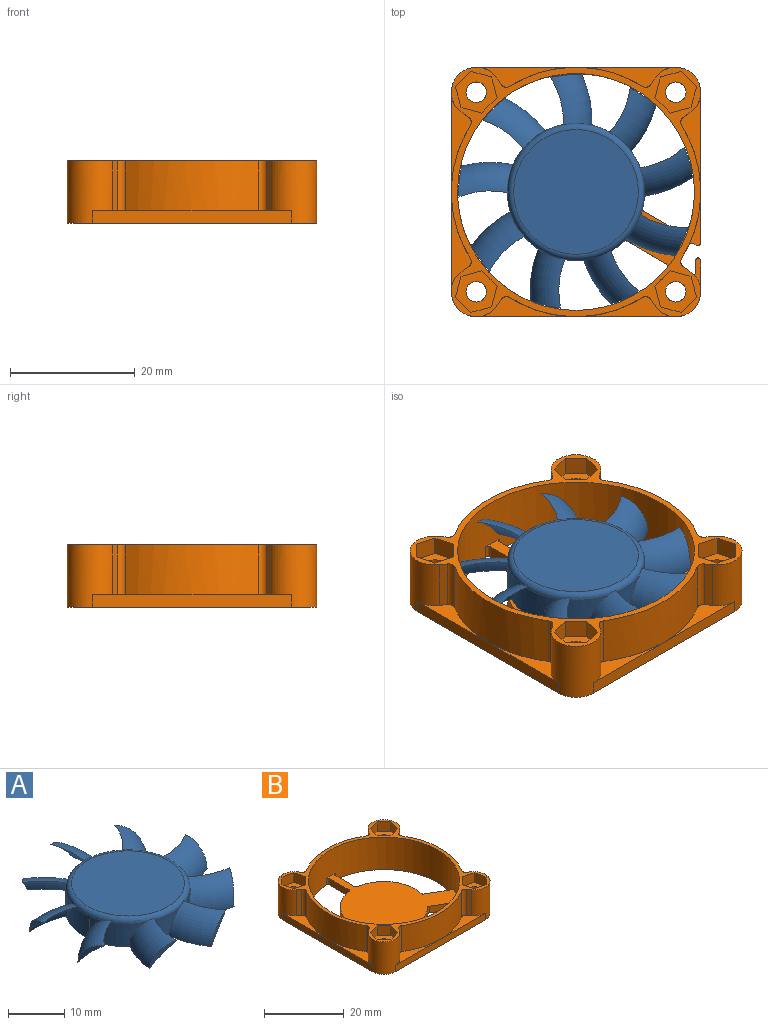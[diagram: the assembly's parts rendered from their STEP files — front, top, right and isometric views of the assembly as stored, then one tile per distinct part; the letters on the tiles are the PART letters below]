
ASSEMBLY  parts=2 mates=1
PART A: 32 faces, bbox 42.3x42.5x6 mm
  f0: cylinder r=11mm len=22mm, axis (0,0,-1), area 307.6mm2, adj f1,f3,f4,f5,f6,f8,f9,f11
  f1: cylinder r=11mm len=4.52mm, axis (0,0,-1), area 3.9mm2, adj f0,f4,f11
  f2: plane 20x20mm, normal (0,0,1), area 314.2mm2, adj f4
  f3: plane 22x22mm, normal (0,0,-1), area 380.1mm2, adj f0
  f4: torus R=10mm, axis (0,0,1), area 102.2mm2, adj f0,f1,f2,f5,f6,f8,f9,f11
  f5: torus R=12.73mm, axis (0,0,-1), area 60.3mm2, adj f0,f4,f6,f7
  f6: torus R=5.4mm, axis (0,0,-1), area 55.4mm2, adj f0,f4,f5,f7
  f7: cylinder r=18.8mm len=4.97mm, axis (0,0,1), area 4.5mm2, adj f5,f6
  f8: torus R=12.73mm, axis (0,0,-1), area 60.3mm2, adj f0,f4,f9,f10
  f9: torus R=5.4mm, axis (0,0,-1), area 55.4mm2, adj f0,f4,f8,f10
  f10: cylinder r=18.8mm len=4.97mm, axis (0,0,1), area 4.5mm2, adj f8,f9
  f11: torus R=12.73mm, axis (0,0,-1), area 60.3mm2, adj f0,f1,f4,f12,f13
  f12: torus R=5.4mm, axis (0,0,-1), area 55.4mm2, adj f0,f4,f11,f13
  f13: cylinder r=18.8mm len=4.97mm, axis (0,0,1), area 4.5mm2, adj f11,f12
  f14: torus R=12.73mm, axis (0,0,-1), area 60.3mm2, adj f0,f4,f15,f16
  f15: torus R=5.4mm, axis (0,0,-1), area 55.4mm2, adj f0,f4,f14,f16
  f16: cylinder r=18.8mm len=4.97mm, axis (0,0,1), area 4.5mm2, adj f14,f15
  f17: torus R=12.73mm, axis (0,0,-1), area 60.3mm2, adj f0,f4,f18,f19
  f18: torus R=5.4mm, axis (0,0,-1), area 55.4mm2, adj f0,f4,f17,f19
  f19: cylinder r=18.8mm len=4.97mm, axis (0,0,1), area 4.5mm2, adj f17,f18
  f20: torus R=12.73mm, axis (0,0,-1), area 60.3mm2, adj f0,f4,f21,f22
  f21: torus R=5.4mm, axis (0,0,-1), area 55.4mm2, adj f0,f4,f20,f22
  f22: cylinder r=18.8mm len=4.99mm, axis (0,0,1), area 4.5mm2, adj f20,f21
  f23: torus R=12.73mm, axis (0,0,-1), area 60.3mm2, adj f0,f4,f24,f25
  f24: torus R=5.4mm, axis (0,0,-1), area 55.4mm2, adj f0,f4,f23,f25
  f25: cylinder r=18.8mm len=4.97mm, axis (0,0,1), area 4.5mm2, adj f23,f24
  f26: torus R=12.73mm, axis (0,0,-1), area 60.3mm2, adj f0,f4,f27,f28
  f27: torus R=5.4mm, axis (0,0,-1), area 55.4mm2, adj f0,f4,f26,f28
  f28: cylinder r=18.8mm len=5mm, axis (0,0,1), area 4.5mm2, adj f26,f27
  f29: torus R=12.73mm, axis (0,0,-1), area 60.3mm2, adj f0,f4,f30,f31
  f30: torus R=5.4mm, axis (0,0,-1), area 55.4mm2, adj f0,f4,f29,f31
  f31: cylinder r=18.8mm len=4.97mm, axis (0,0,1), area 4.5mm2, adj f29,f30
PART B: 115 faces, bbox 40x40x10 mm
  f0: plane 10.28x5.94mm, normal (0.5,0.87,0), area 11.9mm2, adj f19,f33,f35,f80,f81,f82
  f1: plane 2x1.78mm, normal (-1,0,0), area 3.6mm2, adj f8,f33,f81,f97
  f2: plane 16x3.21mm, normal (0,0,1), area 18mm2, adj f26,f27,f56,f57,f100
  f3: plane 16x3.21mm, normal (0,0,1), area 18mm2, adj f25,f26,f65,f69,f106
  f4: plane 16x3.21mm, normal (0,0,1), area 18mm2, adj f21,f22,f34,f60,f102
  f5: plane 16x3.21mm, normal (0,0,1), area 18mm2, adj f23,f24,f62,f63,f104
  f6: plane 16x3.21mm, normal (0,0,1), area 18mm2, adj f27,f28,f57,f58,f101
  f7: plane 35.04x31.24mm, normal (0,0,1), area 457.1mm2, adj f12,f13,f14,f15,f16,f17,f18,f30
  f8: plane 5.45x1.07mm, normal (0,0,1), area 3mm2, adj f1,f28,f29,f81,f96,f97
  f9: plane 16x3.21mm, normal (0,0,1), area 18mm2, adj f22,f23,f61,f62,f103
  f10: plane 8.58x1.89mm, normal (0,0,1), area 5.1mm2, adj f20,f21,f34,f76,f89
  f11: plane 16x3.21mm, normal (0,0,1), area 18mm2, adj f24,f25,f64,f65,f105
  f12: plane 7.04x2mm, normal (1,0,0), area 14.1mm2, adj f7,f33,f87,f92
  f13: cylinder r=19mm len=38mm, axis (0,0,1), area 1168mm2, adj f7,f33,f71,f83,f84,f85,f86,f87
  f14: plane 6.22x3.59mm, normal (0.5,0.87,0), area 14.4mm2, adj f7,f33,f88,f95
  f15: plane 6.09x3.52mm, normal (0.5,-0.87,0), area 14.1mm2, adj f7,f33,f84,f90
  f16: cylinder r=11mm len=16.31mm, axis (0,0,1), area 36.9mm2, adj f7,f33,f90,f94
  f17: plane 6.09x3.52mm, normal (-0.5,0.87,0), area 14.1mm2, adj f7,f33,f85,f91
  f18: plane 7.04x2mm, normal (-1,0,0), area 14.1mm2, adj f7,f33,f86,f93
  f19: cylinder r=11mm len=3.9mm, axis (0,0,1), area 4.4mm2, adj f0,f20,f33,f35,f77
  f20: plane 8.8x5.08mm, normal (-0.5,-0.87,0), area 6.1mm2, adj f10,f19,f33,f76,f77,f78,f89
  f21: plane 24.08x2mm, normal (1,0,0), area 48.2mm2, adj f4,f10,f22,f33,f89
  f22: cylinder r=4mm len=10mm, axis (0,0,1), area 124.5mm2, adj f4,f9,f21,f23,f33,f60,f61,f71
  f23: plane 32x2mm, normal (0,1,0), area 64mm2, adj f5,f9,f22,f24,f33
  f24: cylinder r=4mm len=10mm, axis (0,0,1), area 124.5mm2, adj f5,f11,f23,f25,f33,f63,f64,f71
  f25: plane 32x2mm, normal (-1,0,0), area 64mm2, adj f3,f11,f24,f26,f33
  f26: cylinder r=4mm len=10mm, axis (0,0,1), area 124.5mm2, adj f2,f3,f25,f27,f33,f56,f69,f71
  f27: plane 32x2mm, normal (0,-1,0), area 64mm2, adj f2,f6,f26,f28,f33
  f28: cylinder r=4mm len=10mm, axis (0,0,1), area 124.9mm2, adj f6,f8,f27,f29,f33,f58,f59,f71
  f29: plane 4.96x2mm, normal (1,0,0), area 9.9mm2, adj f8,f28,f33,f96
  f30: plane 6.22x3.59mm, normal (-0.5,-0.87,0), area 14.4mm2, adj f7,f33,f83,f94
  f31: cylinder r=11mm len=15.12mm, axis (0,0,1), area 40.3mm2, adj f7,f33,f91,f93
  f32: cylinder r=11mm len=13.49mm, axis (0,0,1), area 36.9mm2, adj f7,f33,f92,f95
  f33: plane 40x40mm, normal (0,0,-1), area 793.4mm2, adj f0,f1,f12,f13,f14,f15,f16,f17
  f34: cylinder r=20mm len=21.25mm, axis (0,0,1), area 180.4mm2, adj f4,f10,f71,f76,f79,f98,f102
  f35: plane 9.49x8.4mm, normal (0,0,-1), area 34.2mm2, adj f0,f19,f77,f79,f80
  f36: plane 3.35x3mm, normal (-0.26,-0.97,0), area 10.4mm2, adj f37,f70,f71,f75
  f37: plane 3.35x3mm, normal (-0.97,-0.26,0), area 10.4mm2, adj f36,f38,f71,f75
  f38: plane 3x2.45mm, normal (-0.71,0.71,0), area 10.4mm2, adj f37,f39,f71,f75
  f39: plane 3.35x3mm, normal (0.26,0.97,0), area 10.4mm2, adj f38,f40,f71,f75
  f40: plane 3.35x3mm, normal (0.97,0.26,0), area 10.4mm2, adj f39,f70,f71,f75
  f41: plane 3x2.45mm, normal (-0.71,0.71,0), area 10.4mm2, adj f42,f66,f71,f73
  f42: plane 3.35x3mm, normal (0.26,0.97,0), area 10.4mm2, adj f41,f43,f71,f73
  f43: plane 3.35x3mm, normal (0.97,0.26,0), area 10.4mm2, adj f42,f44,f71,f73
  f44: plane 3x2.45mm, normal (0.71,-0.71,0), area 10.4mm2, adj f43,f45,f71,f73
  f45: plane 3.35x3mm, normal (-0.26,-0.97,0), area 10.4mm2, adj f44,f66,f71,f73
  f46: plane 3.35x3mm, normal (-0.97,0.26,0), area 10.4mm2, adj f47,f67,f71,f72
  f47: plane 3.35x3mm, normal (-0.26,0.97,0), area 10.4mm2, adj f46,f48,f71,f72
  f48: plane 3x2.45mm, normal (0.71,0.71,0), area 10.4mm2, adj f47,f49,f71,f72
  f49: plane 3.35x3mm, normal (0.97,-0.26,0), area 10.4mm2, adj f48,f50,f71,f72
  f50: plane 3.35x3mm, normal (0.26,-0.97,0), area 10.4mm2, adj f49,f67,f71,f72
  f51: plane 3x2.45mm, normal (-0.71,-0.71,0), area 10.4mm2, adj f52,f68,f71,f74
  f52: plane 3.35x3mm, normal (-0.97,0.26,0), area 10.4mm2, adj f51,f53,f71,f74
  f53: plane 3.35x3mm, normal (-0.26,0.97,0), area 10.4mm2, adj f52,f54,f71,f74
  f54: plane 3x2.45mm, normal (0.71,0.71,0), area 10.4mm2, adj f53,f55,f71,f74
  f55: plane 3.35x3mm, normal (0.97,-0.26,0), area 10.4mm2, adj f54,f68,f71,f74
  f56: plane 8x1.06mm, normal (0.82,-0.57,0), area 10.4mm2, adj f2,f26,f71,f100
  f57: cylinder r=20mm len=21.25mm, axis (0,0,-1), area 179.2mm2, adj f2,f6,f71,f100,f101
  f58: plane 8x1.06mm, normal (-0.82,-0.57,0), area 10.4mm2, adj f6,f28,f71,f101
  f59: plane 8.5x1.06mm, normal (0.57,0.82,0), area 11mm2, adj f28,f71,f80,f98
  f60: plane 8x1.06mm, normal (0.57,-0.82,0), area 10.4mm2, adj f4,f22,f71,f102
  f61: plane 8x1.06mm, normal (-0.82,0.57,0), area 10.4mm2, adj f9,f22,f71,f103
  f62: cylinder r=20mm len=21.25mm, axis (0,0,-1), area 179.2mm2, adj f5,f9,f71,f103,f104
  f63: plane 8x1.06mm, normal (0.82,0.57,0), area 10.4mm2, adj f5,f24,f71,f104
  f64: plane 8x1.06mm, normal (-0.57,-0.82,0), area 10.4mm2, adj f11,f24,f71,f105
  f65: cylinder r=20mm len=21.25mm, axis (0,0,-1), area 179.2mm2, adj f3,f11,f71,f105,f106
  f66: plane 3.35x3mm, normal (-0.97,-0.26,0), area 10.4mm2, adj f41,f45,f71,f73
  f67: plane 3x2.45mm, normal (-0.71,-0.71,0), area 10.4mm2, adj f46,f50,f71,f72
  f68: plane 3.35x3mm, normal (0.26,-0.97,0), area 10.4mm2, adj f51,f55,f71,f74
  f69: plane 8x1.06mm, normal (-0.57,0.82,0), area 10.4mm2, adj f3,f26,f71,f106
  f70: plane 3x2.45mm, normal (0.71,-0.71,0), area 10.4mm2, adj f36,f40,f71,f75
  f71: plane 40x40mm, normal (0,0,1), area 183.3mm2, adj f13,f22,f24,f26,f28,f34,f36,f37
  f72: plane 6.69x6.69mm, normal (0,0,1), area 22.6mm2, adj f46,f47,f48,f49,f50,f67,f111
  f73: plane 6.69x6.69mm, normal (0,0,1), area 22.6mm2, adj f41,f42,f43,f44,f45,f66,f109
  f74: plane 6.69x6.69mm, normal (0,0,1), area 22.6mm2, adj f51,f52,f53,f54,f55,f68,f107
  f75: plane 6.69x6.69mm, normal (0,0,1), area 22.6mm2, adj f36,f37,f38,f39,f40,f70,f113
  f76: cylinder r=0.5mm len=0.7mm, axis (0,0,1), area 0.4mm2, adj f10,f20,f34,f78
  f77: cylinder r=0.5mm len=7.74mm, axis (0.87,-0.5,0), area 6.8mm2, adj f19,f20,f35,f78
  f78: bspline ~1.22x1.19mm, area 0.9mm2, adj f20,f76,f77,f79
  f79: torus R=19.5mm, axis (0,0,1), area 2.5mm2, adj f34,f35,f78,f99
  f80: cylinder r=0.5mm len=2.57mm, axis (0.82,-0.57,0), area 1.5mm2, adj f0,f35,f59,f82,f99
  f81: cylinder r=0.5mm len=2mm, axis (0,0,-1), area 1.7mm2, adj f0,f1,f8,f28,f33,f82
  f82: torus R=3.5mm, axis (0,0,1), area 0.4mm2, adj f0,f28,f80,f81
  f83: cylinder r=0.5mm len=2mm, axis (0,0,1), area 1.7mm2, adj f7,f13,f30,f33
  f84: cylinder r=0.5mm len=2mm, axis (0,0,1), area 1.7mm2, adj f7,f13,f15,f33
  f85: cylinder r=0.5mm len=2mm, axis (0,0,1), area 1.7mm2, adj f7,f13,f17,f33
  f86: cylinder r=0.5mm len=2mm, axis (0,0,1), area 1.7mm2, adj f7,f13,f18,f33
  f87: cylinder r=0.5mm len=2mm, axis (0,0,1), area 1.7mm2, adj f7,f12,f13,f33
  f88: cylinder r=0.5mm len=2mm, axis (0,0,1), area 1.7mm2, adj f7,f13,f14,f33
  f89: cylinder r=0.5mm len=2mm, axis (0,0,-1), area 2.1mm2, adj f10,f20,f21,f33
  f90: cylinder r=0.5mm len=2mm, axis (0,0,1), area 1.4mm2, adj f7,f15,f16,f33
  f91: cylinder r=0.5mm len=2mm, axis (0,0,1), area 1.4mm2, adj f7,f17,f31,f33
  f92: cylinder r=0.5mm len=2mm, axis (0,0,1), area 1.4mm2, adj f7,f12,f32,f33
  f93: cylinder r=0.5mm len=2mm, axis (0,0,1), area 1.4mm2, adj f7,f18,f31,f33
  f94: cylinder r=0.5mm len=2mm, axis (0,0,1), area 1.3mm2, adj f7,f16,f30,f33
  f95: cylinder r=0.5mm len=2mm, axis (0,0,1), area 1.3mm2, adj f7,f14,f32,f33
  f96: cylinder r=0.5mm len=2mm, axis (0,0,1), area 1.4mm2, adj f8,f29,f33,f97
  f97: cylinder r=0.5mm len=2mm, axis (0,0,1), area 1.4mm2, adj f1,f8,f33,f96
  f98: cylinder r=1mm len=8.5mm, axis (0,0,1), area 12.9mm2, adj f34,f59,f71,f99
  f99: bspline ~1.5x1.35mm, area 0.5mm2, adj f79,f80,f98
  f100: cylinder r=1mm len=8mm, axis (0,0,-1), area 12.2mm2, adj f2,f56,f57,f71
  f101: cylinder r=1mm len=8mm, axis (0,0,-1), area 12.2mm2, adj f6,f57,f58,f71
  f102: cylinder r=1mm len=8mm, axis (0,0,1), area 12.2mm2, adj f4,f34,f60,f71
  f103: cylinder r=1mm len=8mm, axis (0,0,-1), area 12.2mm2, adj f9,f61,f62,f71
  f104: cylinder r=1mm len=8mm, axis (0,0,-1), area 12.2mm2, adj f5,f62,f63,f71
  f105: cylinder r=1mm len=8mm, axis (0,0,-1), area 12.2mm2, adj f11,f64,f65,f71
  f106: cylinder r=1mm len=8mm, axis (0,0,-1), area 12.2mm2, adj f3,f65,f69,f71
  f107: cylinder r=1.65mm len=6.4mm, axis (0,0,-1), area 66.4mm2, adj f74,f108
  f108: cone r=1.65mm half-angle=45deg, axis (0,0,-1), area 10.4mm2, adj f33,f107
  f109: cylinder r=1.65mm len=6.4mm, axis (0,0,-1), area 66.4mm2, adj f73,f110
  f110: cone r=1.65mm half-angle=45deg, axis (0,0,-1), area 10.4mm2, adj f33,f109
  f111: cylinder r=1.65mm len=6.4mm, axis (0,0,-1), area 66.4mm2, adj f72,f112
  f112: cone r=1.65mm half-angle=45deg, axis (0,0,-1), area 10.4mm2, adj f33,f111
  f113: cylinder r=1.65mm len=6.4mm, axis (0,0,-1), area 66.4mm2, adj f75,f114
  f114: cone r=1.65mm half-angle=45deg, axis (0,0,-1), area 10.4mm2, adj f33,f113
PLACE A rot(axis=(0,0,-1),109.7deg) t=(0,0,0)mm
PLACE B at identity fixed
MATE revolute A.f0 <-> B.f13  axis (0,0,-1) through (0,0,0)mm
